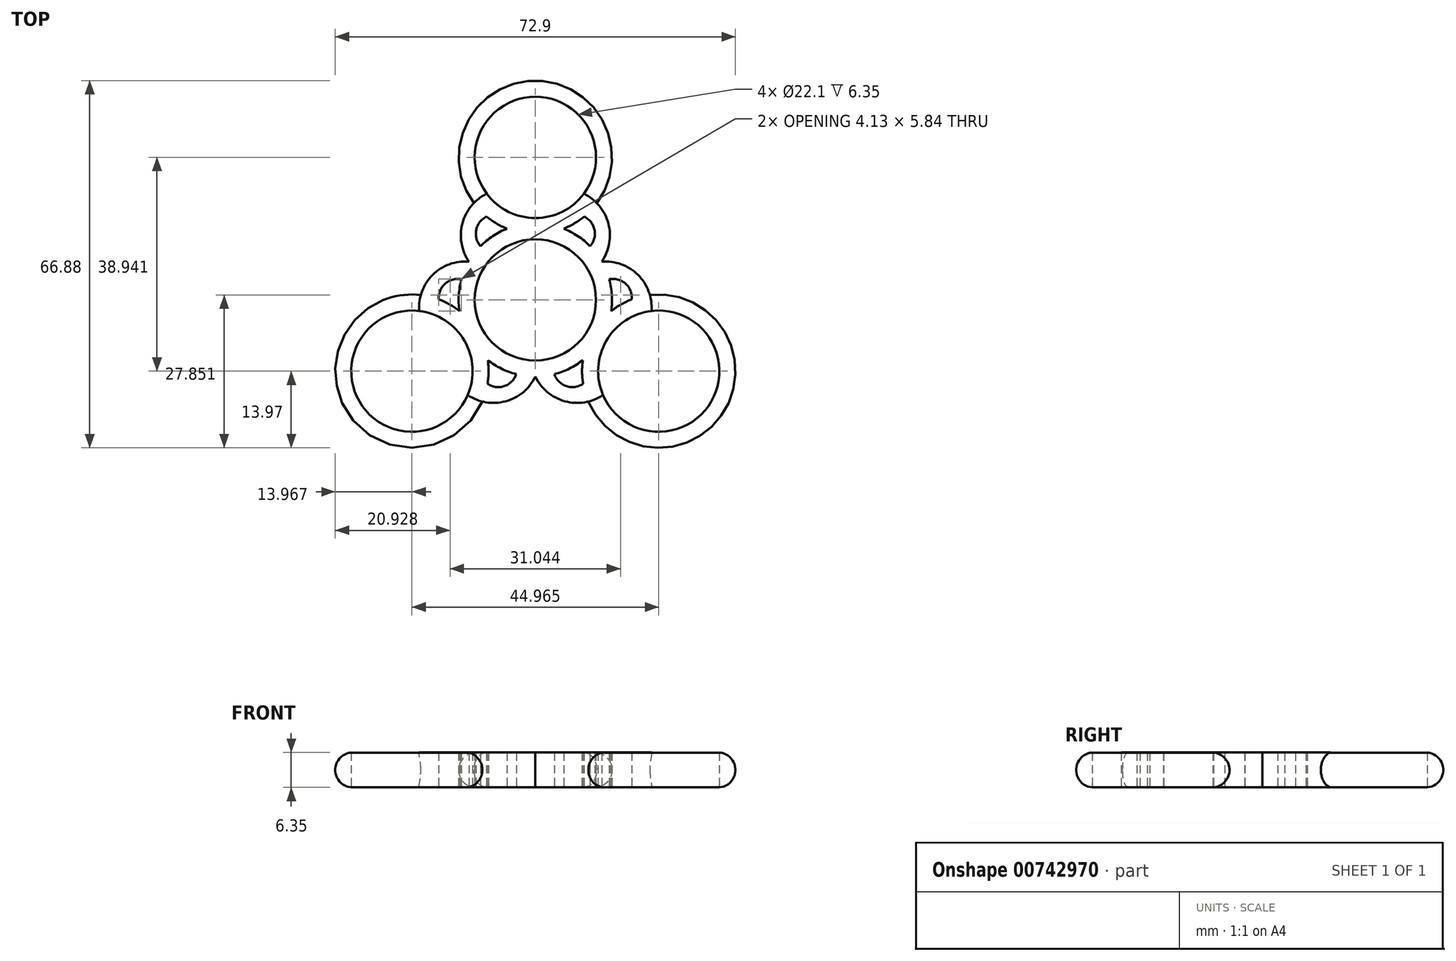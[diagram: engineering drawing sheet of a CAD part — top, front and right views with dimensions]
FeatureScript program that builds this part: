
annotation { "Feature Type Name" : "Feature", "Feature Type Description" : "" }
export const myFeature = defineFeature(function(context is Context, id is Id, definition is map)
    precondition{}
    {
        {
            var Q0;
            Q0=qCreatedBy(makeId("Top.planeOp"),FACE);
            var sketch = newSketch(context, id + "F0", { "sketchPlane" : qUnion([Q0])});
            skCircle(sketch, "E0", {"center": v(0, 0) * mm, "radius": 11.05 * mm});
            skArc(sketch, "E1", {"start": v(-5.16, 12.98) * mm, "mid": v(-7.74, 11.63) * mm, "end": v(-9.98, 9.78) * mm});
            skCircle(sketch, "E2", {"center": v(0, 25.96) * mm, "radius": 11.05 * mm});
            skArc(sketch, "E3", {"start": v(5.16, 12.98) * mm, "mid": v(7.1, 13.93) * mm, "end": v(8.88, 15.18) * mm});
            skCircle(sketch, "E4.1.1", {"center": v(-22.48, -12.98) * mm, "radius": 11.05 * mm});
            skArc(sketch, "E4.2.0", {"start": v(8.66, -10.96) * mm, "mid": v(8.51, -13.12) * mm, "end": v(8.7, -15.28) * mm});
            skCircle(sketch, "E4.2.1", {"center": v(22.48, -12.98) * mm, "radius": 11.05 * mm});
            skArc(sketch, "E5.trimOffspring", {"start": v(-8.66, -10.96) * mm, "mid": v(-6.2, -12.52) * mm, "end": v(-3.48, -13.53) * mm});
            skArc(sketch, "E6.trimOffspring", {"start": v(13.82, -2.02) * mm, "mid": v(13.94, 0.89) * mm, "end": v(13.46, 3.75) * mm});
            skArc(sketch, "E7", {"start": v(-8.88, 15.18) * mm, "mid": v(-10.78, 12.75) * mm, "end": v(-9.98, 9.78) * mm});
            skArc(sketch, "E8", {"start": v(-11.2, 17.62) * mm, "mid": v(-13.55, 12.46) * mm, "end": v(-12.1, 6.99) * mm});
            skArc(sketch, "E9.trimOffspring", {"start": v(-8.88, 15.18) * mm, "mid": v(-7.1, 13.93) * mm, "end": v(-5.16, 12.98) * mm});
            skArc(sketch, "E10.trimOffspring", {"start": v(-13.46, 3.75) * mm, "mid": v(-13.94, 0.89) * mm, "end": v(-13.82, -2.02) * mm});
            skArc(sketch, "E11.MirrorCS", {"start": v(8.88, 15.18) * mm, "mid": v(10.78, 12.75) * mm, "end": v(9.98, 9.78) * mm});
            skArc(sketch, "E12.MirrorCS", {"start": v(11.2, 17.62) * mm, "mid": v(13.55, 12.46) * mm, "end": v(12.1, 6.99) * mm});
            skArc(sketch, "E13.trimOffspring", {"start": v(11.2, 17.62) * mm, "mid": v(0, 39.93) * mm, "end": v(-11.2, 17.62) * mm});
            skArc(sketch, "E14.trimOffspring", {"start": v(9.98, 9.78) * mm, "mid": v(7.74, 11.63) * mm, "end": v(5.16, 12.98) * mm});
            skArc(sketch, "E15.1.0", {"start": v(-8.7, -15.28) * mm, "mid": v(-5.65, -15.7) * mm, "end": v(-3.48, -13.53) * mm});
            skArc(sketch, "E15.1.1", {"start": v(-9.66, -18.52) * mm, "mid": v(-4.02, -17.96) * mm, "end": v(0, -13.97) * mm});
            skArc(sketch, "E15.1.2", {"start": v(-17.59, 0.1) * mm, "mid": v(-16.43, 2.96) * mm, "end": v(-13.46, 3.75) * mm});
            skArc(sketch, "E15.1.3", {"start": v(-20.87, 0.9) * mm, "mid": v(-17.56, 5.5) * mm, "end": v(-12.1, 6.99) * mm});
            skArc(sketch, "E15.2.0", {"start": v(17.59, 0.1) * mm, "mid": v(16.43, 2.96) * mm, "end": v(13.46, 3.75) * mm});
            skArc(sketch, "E15.2.1", {"start": v(20.87, 0.9) * mm, "mid": v(17.56, 5.5) * mm, "end": v(12.1, 6.98) * mm});
            skArc(sketch, "E15.2.2", {"start": v(8.7, -15.28) * mm, "mid": v(5.65, -15.7) * mm, "end": v(3.48, -13.53) * mm});
            skArc(sketch, "E15.2.3", {"start": v(9.66, -18.52) * mm, "mid": v(4.02, -17.96) * mm, "end": v(0, -13.97) * mm});
            skArc(sketch, "E16.trimOffspring", {"start": v(-20.87, 0.9) * mm, "mid": v(-34.58, -19.97) * mm, "end": v(-9.66, -18.52) * mm});
            skArc(sketch, "E17.trimOffspring", {"start": v(17.59, 0.1) * mm, "mid": v(15.62, -0.81) * mm, "end": v(13.82, -2.02) * mm});
            skArc(sketch, "E18.trimOffspring", {"start": v(-8.7, -15.28) * mm, "mid": v(-8.51, -13.12) * mm, "end": v(-8.66, -10.96) * mm});
            skArc(sketch, "E19.trimOffspring", {"start": v(3.48, -13.53) * mm, "mid": v(6.2, -12.52) * mm, "end": v(8.66, -10.96) * mm});
            skArc(sketch, "E20.trimOffspring", {"start": v(9.66, -18.52) * mm, "mid": v(34.58, -19.97) * mm, "end": v(20.87, 0.9) * mm});
            skArc(sketch, "E21.MirrorCS", {"start": v(-17.59, 0.1) * mm, "mid": v(-15.62, -0.81) * mm, "end": v(-13.82, -2.02) * mm});
            skSolve(sketch);
        }
        {
            var Q0;
            Q0 = qSketchRegion(id + "F0", true);
            extrude(context, id + "F1", {"entities" : qUnion([Q0]), "depth" : 6.35 * mm, "offsetDistance" : 25.4 * mm});
        }
        {
            var Q0;
            Q0=makeQuery(id+"F1.opExtrude","CAP_EDGE",EDGE,{"disambiguationData":[OSD([sQuery(id+"F0.wireOp",EDGE,"E13.trimOffspring")])],"isStart":false});
            var Q1;
            Q1=makeQuery(id+"F1.opExtrude","CAP_EDGE",EDGE,{"disambiguationData":[OSD([sQuery(id+"F0.wireOp",EDGE,"E16.trimOffspring")])],"isStart":false});
            var Q2;
            Q2=makeQuery(id+"F1.opExtrude","CAP_EDGE",EDGE,{"disambiguationData":[OSD([sQuery(id+"F0.wireOp",EDGE,"E20.trimOffspring")])],"isStart":false});
            var Q3;
            Q3=makeQuery(id+"F1.opExtrude","CAP_EDGE",EDGE,{"disambiguationData":[OSD([sQuery(id+"F0.wireOp",EDGE,"E20.trimOffspring")])],"isStart":true});
            var Q4;
            Q4=makeQuery(id+"F1.opExtrude","CAP_EDGE",EDGE,{"disambiguationData":[OSD([sQuery(id+"F0.wireOp",EDGE,"E16.trimOffspring")])],"isStart":true});
            var Q5;
            Q5=makeQuery(id+"F1.opExtrude","CAP_EDGE",EDGE,{"disambiguationData":[OSD([sQuery(id+"F0.wireOp",EDGE,"E13.trimOffspring")])],"isStart":true});
            fillet(context, id + "F2", {"entities" : qUnion([Q0, Q1, Q2, Q3, Q4, Q5]), "radius" : 3.17 * mm, "tangentPropagation" : true, "allowEdgeOverflow" : false});
        }
    });
